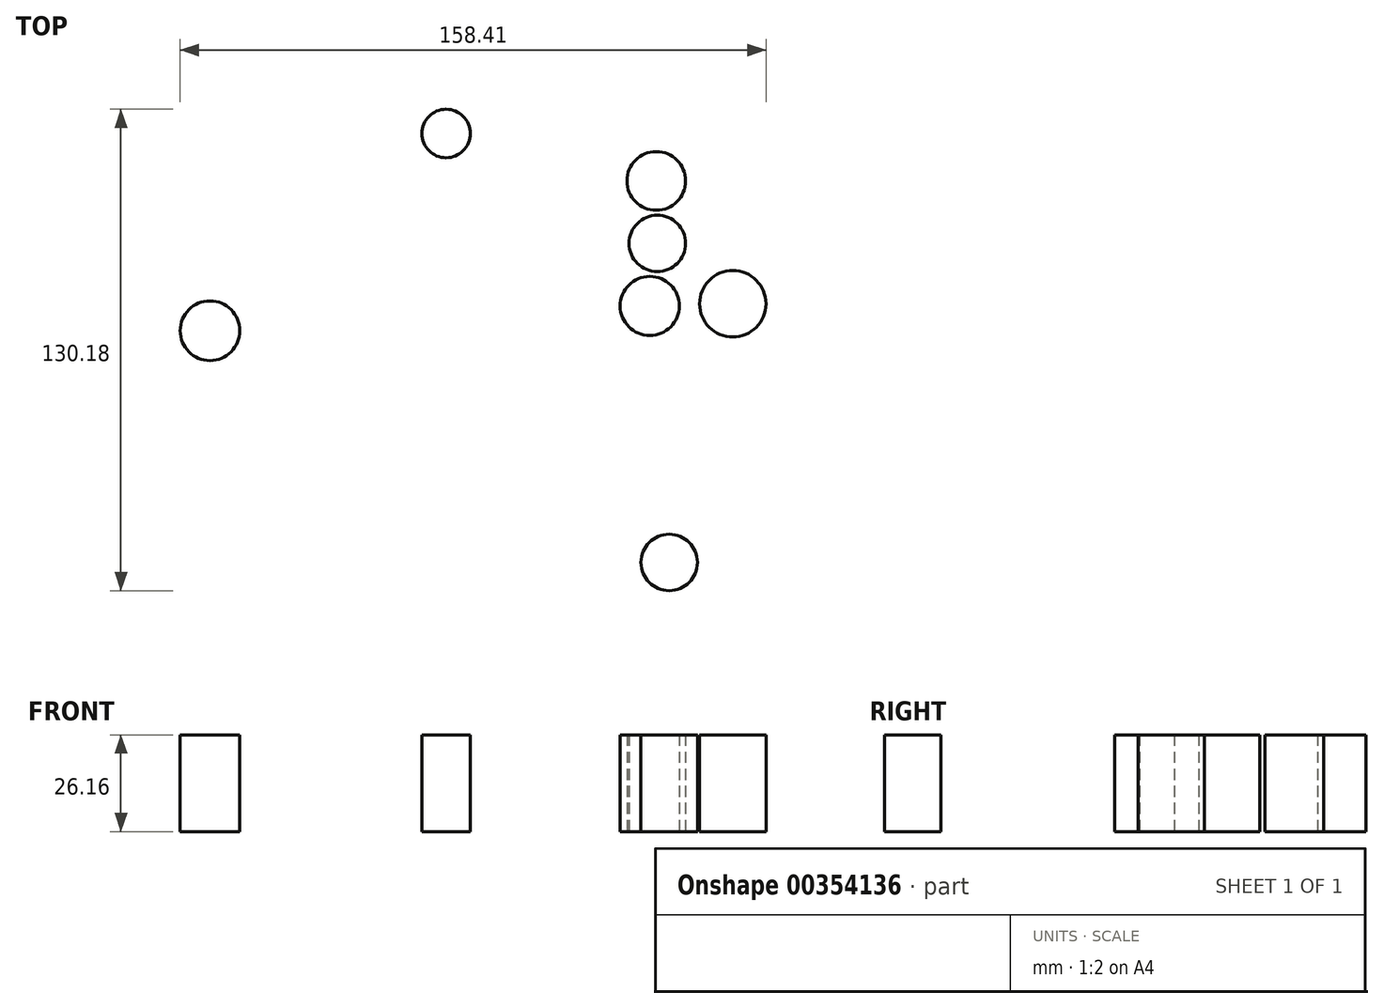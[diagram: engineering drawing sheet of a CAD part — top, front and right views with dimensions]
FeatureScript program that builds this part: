
annotation { "Feature Type Name" : "Feature", "Feature Type Description" : "" }
export const myFeature = defineFeature(function(context is Context, id is Id, definition is map)
    precondition{}
    {
        {
            var Q0;
            Q0=qCreatedBy(makeId("Top.planeOp"),FACE);
            var sketch = newSketch(context, id + "F0", { "sketchPlane" : qUnion([Q0])});
            skCircle(sketch, "E0", {"center": v(24.78, 52.03) * mm, "radius": 7.93 * mm});
            skCircle(sketch, "E1", {"center": v(25.07, 35.12) * mm, "radius": 7.63 * mm});
            skCircle(sketch, "E2", {"center": v(23.03, 18.22) * mm, "radius": 8 * mm});
            skCircle(sketch, "E3", {"center": v(45.47, 18.8) * mm, "radius": 8.98 * mm});
            skCircle(sketch, "E4", {"center": v(28.27, -51.15) * mm, "radius": 7.63 * mm});
            skCircle(sketch, "E5", {"center": v(-32.06, 64.85) * mm, "radius": 6.55 * mm});
            skCircle(sketch, "E6", {"center": v(-95.9, 11.51) * mm, "radius": 8.06 * mm});
            skSolve(sketch);
        }
        {
            var Q0;
            Q0 = qSketchRegion(id + "F0", true);
            extrude(context, id + "F1", {"entities" : qUnion([Q0]), "depth" : 26.16 * mm});
        }
    });
